# Revit family: 5304a_rj45_and_cat5
name_source: partatom
category: Communication Devices
revit_build: Autodesk Revit 2014 (Build: 20130308_1515(x64)
units: mm (PartAtom-declared; Revit-internal decimal feet)

## types (1)
- 5304a_rj45_and_cat5
    Assembly Code = D5090
    Black = Paint - Hubbell - Carbon Black
    Certificatins = cULus listed
    Default Elevation = 48 "
    Description = The Hubbell Control Solutions NXFSP and NXDSP dual SmartPORT™ adapters allow for wired CAT5 interconnection of luminaires equipped with internal NXFM In-fixture modules.
    Electrical Parameters = RJ45ADAPTER: 4 Terminal Connectors
 Red: +24V
Blue: Occupancy Sensor Input
Yellow: Photocell/Daylight Sensor Input
Black: Common
Class 2 device
Max Cable Length Supported: 300 ft. from device to control module
    Green = Plastic - Hubbell - Green
    Height = 18.26 "
    Manufacturer = Hubbell Control Solutions
    Model = RJ45 Adapter and CAT5 System Cables
    Product Documentation Link = https://hubbellcdn.com
    Product Page URL = https://www.hubbell.com
    Type Comments = RJ45 Adapter and CAT5 System Cables
    URL = https://www.hubbell.com
    Warranty = 5-Years Warranty
    White = Plastic - Hubbell - Gray
    Width = 14.5 "

## geometry (parser evidence)
native form markers: Sweep x1
no freeform markers — native parametric forms only
